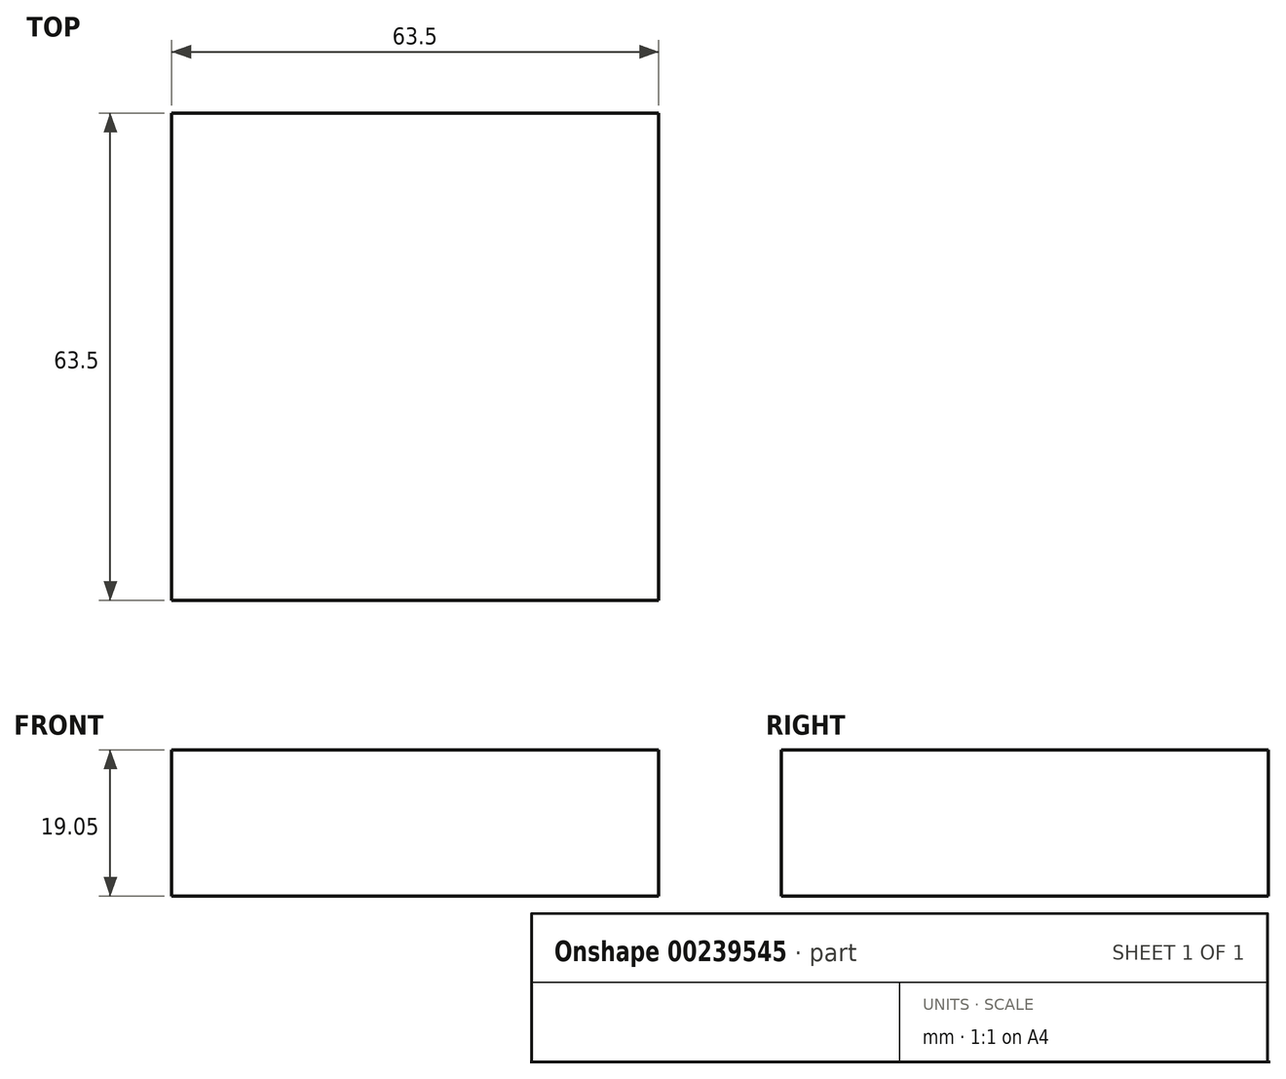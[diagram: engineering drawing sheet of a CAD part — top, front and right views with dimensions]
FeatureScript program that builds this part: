
annotation { "Feature Type Name" : "Feature", "Feature Type Description" : "" }
export const myFeature = defineFeature(function(context is Context, id is Id, definition is map)
    precondition{}
    {
        {
            var Q0;
            Q0=qCreatedBy(makeId("Top.planeOp"),FACE);
            var sketch = newSketch(context, id + "F0", { "sketchPlane" : qUnion([Q0])});
            skLineSegment(sketch, "E0.bottom", {"start": v(31.75, 31.75) * mm, "end": v(-31.75, 31.75) * mm});
            skLineSegment(sketch, "E0.top", {"start": v(31.75, -31.75) * mm, "end": v(-31.75, -31.75) * mm});
            skLineSegment(sketch, "E0.left", {"start": v(31.75, 31.75) * mm, "end": v(31.75, -31.75) * mm});
            skLineSegment(sketch, "E0.right", {"start": v(-31.75, 31.75) * mm, "end": v(-31.75, -31.75) * mm});
            skPoint(sketch, "E0.middle", {"position": v(0, 0) * mm});
            skSolve(sketch);
        }
        {
            var Q0;
            Q0 = qSketchRegion(id + "F0", true);
            extrude(context, id + "F1", {"entities" : qUnion([Q0]), "depth" : 19.05 * mm});
        }
    });
